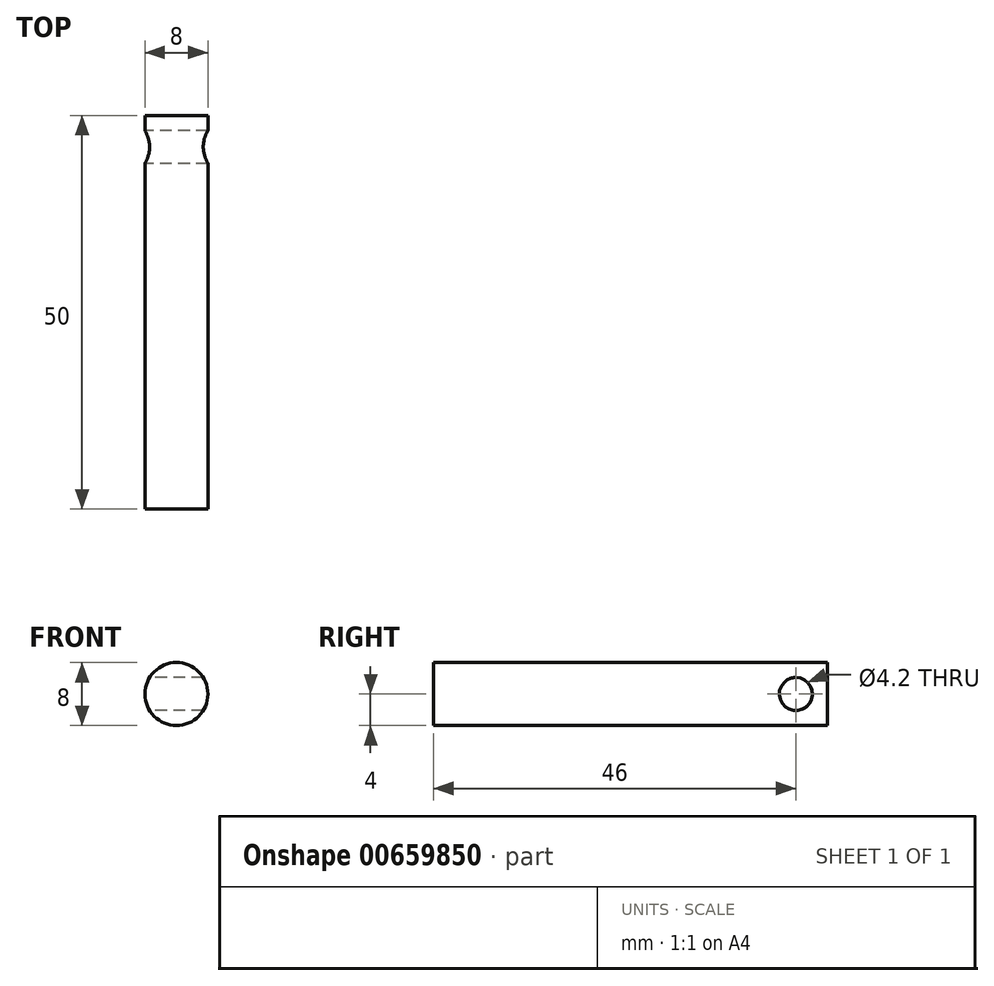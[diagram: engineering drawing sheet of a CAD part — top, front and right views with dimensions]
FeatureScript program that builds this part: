
annotation { "Feature Type Name" : "Feature", "Feature Type Description" : "" }
export const myFeature = defineFeature(function(context is Context, id is Id, definition is map)
    precondition{}
    {
        {
            var Q0;
            Q0=qCreatedBy(makeId("Front.planeOp"),FACE);
            var sketch = newSketch(context, id + "F0", { "sketchPlane" : qUnion([Q0])});
            skCircle(sketch, "E0", {"center": v(0, 0) * mm, "radius": 4 * mm});
            skSolve(sketch);
        }
        {
            var Q0;
            Q0=makeQuery(id+"F0.imprint","IMPRINT",FACE,{"disambiguationData":[TD([[makeQuery(id+"F0.imprint","IMPRINT",EDGE,{"derivedFrom":sQuery(id+"F0.wireOp",EDGE,"E0")}),1.0]])]});
            extrude(context, id + "F1", {"entities" : qUnion([Q0]), "depth" : 50 * mm, "offsetDistance" : 25 * mm});
        }
        {
            var Q0;
            Q0=qCreatedBy(makeId("Right.planeOp"),FACE);
            var sketch = newSketch(context, id + "F2", { "sketchPlane" : qUnion([Q0])});
            skPoint(sketch, "E1", {"position": v(-4, 0) * mm});
            skCircle(sketch, "E2", {"center": v(-4, 0) * mm, "radius": 2.1 * mm});
            skSolve(sketch);
        }
        {
            var Q0;
            Q0 = qSketchRegion(id + "F2", true);
            extrude(context, id + "F3", {"entities" : qUnion([Q0]), "operationType" : NewBodyOperationType.REMOVE, "endBound" : BoundingType.SYMMETRIC, "depth" : 100 * mm, "offsetDistance" : 25 * mm});
        }
    });
